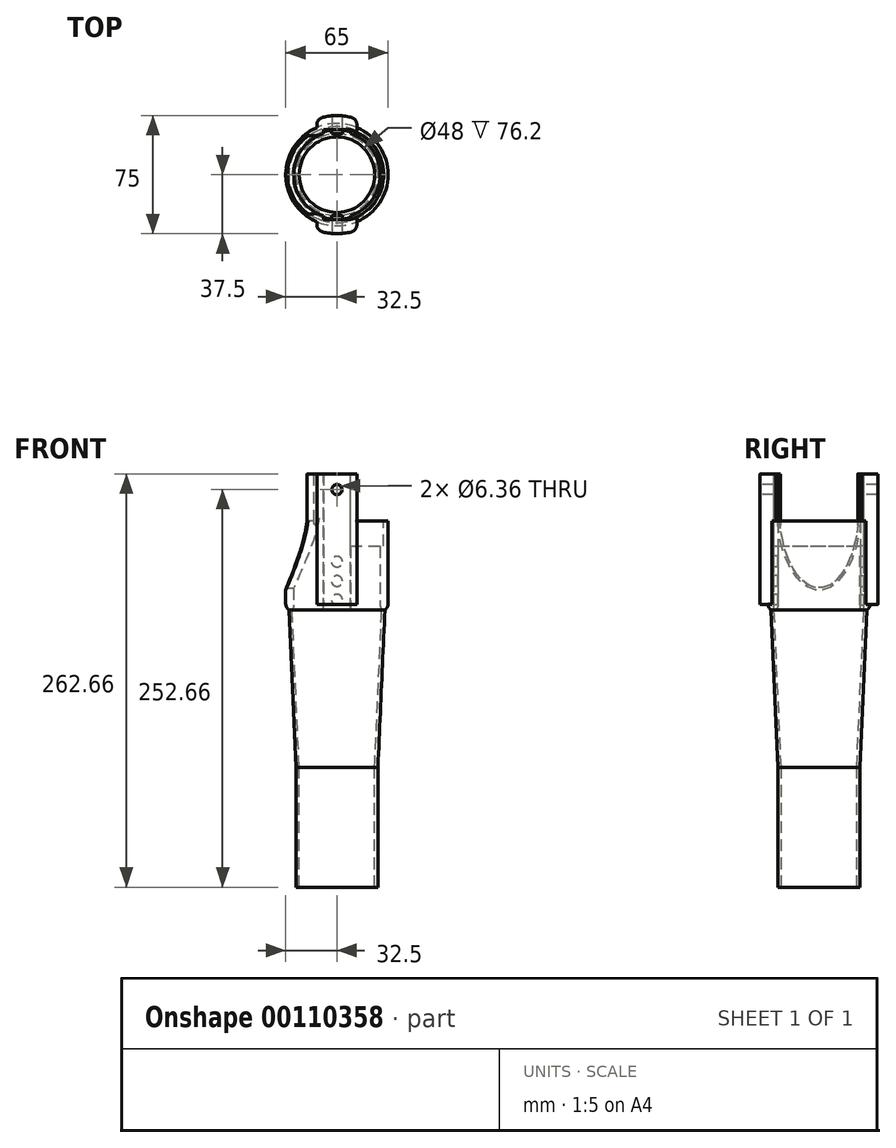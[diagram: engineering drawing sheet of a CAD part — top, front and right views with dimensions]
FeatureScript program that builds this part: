
annotation { "Feature Type Name" : "Feature", "Feature Type Description" : "" }
export const myFeature = defineFeature(function(context is Context, id is Id, definition is map)
    precondition{}
    {
        {
            var Q0;
            Q0=qCreatedBy(makeId("Top.planeOp"),FACE);
            var sketch = newSketch(context, id + "F0", { "sketchPlane" : qUnion([Q0])});
            skCircle(sketch, "E0", {"center": v(0, 0) * mm, "radius": 26 * mm});
            skSolve(sketch);
        }
        {
            var Q0;
            Q0=makeQuery(id+"F0.imprint","IMPRINT",FACE,{"disambiguationData":[TD([[makeQuery(id+"F0.imprint","IMPRINT",EDGE,{"derivedFrom":sQuery(id+"F0.wireOp",EDGE,"E0")}),1.0]])]});
            extrude(context, id + "F1", {"entities" : qUnion([Q0]), "depth" : 76.2 * mm});
        }
        {
            var Q0;
            Q0=makeQuery(id+"F1.opExtrude","CAP_FACE",FACE,{"disambiguationData":[OSD([sQuery(id+"F0.wireOp",EDGE,"E0")])],"isStart":false});
            cPlane(context, id + "F2", {"entities" : qUnion([Q0]), "cplaneType" : CPlaneType.OFFSET, "offset" : 0 * mm, "width" : 150 * mm, "height" : 150 * mm});
        }
        {
            var Q0;
            Q0=qCreatedBy(id+"F2.planeOp",FACE);
            var sketch = newSketch(context, id + "F3", { "sketchPlane" : qUnion([Q0])});
            skCircle(sketch, "E1.0", {"center": v(0, 0) * mm, "radius": 26 * mm});
            skSolve(sketch);
        }
        {
            var Q0;
            Q0=qCreatedBy(id+"F2.planeOp",FACE);
            cPlane(context, id + "F4", {"entities" : qUnion([Q0]), "cplaneType" : CPlaneType.OFFSET, "offset" : 100 * mm, "width" : 150 * mm, "height" : 150 * mm});
        }
        {
            var Q0;
            Q0=qCreatedBy(id+"F4.planeOp",FACE);
            var sketch = newSketch(context, id + "F5", { "sketchPlane" : qUnion([Q0])});
            skCircle(sketch, "E2", {"center": v(0, 0) * mm, "radius": 30.5 * mm});
            skSolve(sketch);
        }
        {
            var Q1;
            Q1=makeQuery(id+"F3.imprint","IMPRINT",FACE,{"disambiguationData":[TD([[makeQuery(id+"F3.imprint","IMPRINT",EDGE,{"derivedFrom":sQuery(id+"F3.wireOp",EDGE,"E1.0")}),1.0]])]});
            var Q2;
            Q2=makeQuery(id+"F5.imprint","IMPRINT",FACE,{"disambiguationData":[TD([[makeQuery(id+"F5.imprint","IMPRINT",EDGE,{"derivedFrom":sQuery(id+"F5.wireOp",EDGE,"E2")}),1.0]])]});
            loft(context, id + "F6", {"operationType" : NewBodyOperationType.ADD, "sheetProfilesArray" : [{ "sheetProfileEntities" : qUnion([Q1]) }, { "sheetProfileEntities" : qUnion([Q2]) }]});
        }
        {
            var Q0;
            Q0=qCreatedBy(id+"F2.planeOp",FACE);
            var sketch = newSketch(context, id + "F7", { "sketchPlane" : qUnion([Q0])});
            skCircle(sketch, "E3", {"center": v(0, 0) * mm, "radius": 24 * mm});
            skSolve(sketch);
        }
        {
            var Q0;
            Q0=qCreatedBy(id+"F4.planeOp",FACE);
            var sketch = newSketch(context, id + "F8", { "sketchPlane" : qUnion([Q0])});
            skCircle(sketch, "E4", {"center": v(0, 0) * mm, "radius": 28.5 * mm});
            skSolve(sketch);
        }
        {
            var Q1;
            Q1=makeQuery(id+"F8.imprint","IMPRINT",FACE,{"disambiguationData":[TD([[makeQuery(id+"F8.imprint","IMPRINT",EDGE,{"derivedFrom":sQuery(id+"F8.wireOp",EDGE,"E4")}),1.0]])]});
            var Q2;
            Q2=qSketchRegion(id+"F7",true);
            loft(context, id + "F9", {"operationType" : NewBodyOperationType.REMOVE, "sheetProfilesArray" : [{ "sheetProfileEntities" : qUnion([Q1]) }, { "sheetProfileEntities" : qUnion([Q2]) }]});
        }
        {
            var Q0;
            Q0=qCreatedBy(makeId("Top.planeOp"),FACE);
            var sketch = newSketch(context, id + "F10", { "sketchPlane" : qUnion([Q0])});
            skCircle(sketch, "E5", {"center": v(0, 0) * mm, "radius": 24 * mm});
            skSolve(sketch);
        }
        {
            var Q1;
            Q1=qSketchRegion(id+"F7",true);
            var Q2;
            Q2=qSketchRegion(id+"F10",true);
            loft(context, id + "F11", {"operationType" : NewBodyOperationType.REMOVE, "sheetProfilesArray" : [{ "sheetProfileEntities" : qUnion([Q1]) }, { "sheetProfileEntities" : qUnion([Q2]) }]});
        }
        {
            var Q0;
            Q0=qCreatedBy(id+"F4.planeOp",FACE);
            var sketch = newSketch(context, id + "F12", { "sketchPlane" : qUnion([Q0])});
            skCircle(sketch, "E6", {"center": v(0, 0) * mm, "radius": 32.5 * mm});
            skCircle(sketch, "E7.0", {"center": v(0, 0) * mm, "radius": 27.5 * mm});
            skSolve(sketch);
        }
        {
            var Q0;
            Q0=qSketchRegion(id+"F12",true);
            extrude(context, id + "F13", {"entities" : qUnion([Q0]), "operationType" : NewBodyOperationType.ADD, "depth" : 56.46 * mm});
        }
        {
            var Q0;
            Q0=makeQuery(id+"F13.opExtrude","CAP_EDGE",EDGE,{"disambiguationData":[OSD([sQuery(id+"F12.wireOp",EDGE,"E6")])],"isStart":true});
            fillet(context, id + "F14", {"entities" : qUnion([Q0]), "radius" : 5 * mm, "tangentPropagation" : true, "allowEdgeOverflow" : false});
        }
        {
            var Q0;
            Q0=makeQuery(id+"F13.opExtrude","CAP_FACE",FACE,{"disambiguationData":[OSD([sQuery(id+"F12.wireOp",EDGE,"E6"),sQuery(id+"F12.wireOp",EDGE,"E7.0")])],"isStart":false});
            cPlane(context, id + "F15", {"entities" : qUnion([Q0]), "cplaneType" : CPlaneType.OFFSET, "offset" : 0 * mm, "width" : 150 * mm, "height" : 150 * mm});
        }
        {
            var Q0;
            Q0=qCreatedBy(id+"F15.planeOp",FACE);
            var sketch = newSketch(context, id + "F16", { "sketchPlane" : qUnion([Q0])});
            skCircle(sketch, "E8.0", {"center": v(0, 0) * mm, "radius": 32.5 * mm, "construction": true});
            skCircle(sketch, "E9.0", {"center": v(0, 0) * mm, "radius": 27.5 * mm, "construction": true});
            skArc(sketch, "E10", {"start": v(8.5, -28.5) * mm, "mid": v(29.74, 0) * mm, "end": v(8.5, 28.5) * mm});
            skArc(sketch, "E11", {"start": v(8.5, -24.3) * mm, "mid": v(25.75, 0) * mm, "end": v(8.5, 24.3) * mm});
            skLineSegment(sketch, "E12", {"start": v(8.5, 28.5) * mm, "end": v(8.5, 24.3) * mm});
            skLineSegment(sketch, "E13.MirrorCS", {"start": v(8.5, -28.5) * mm, "end": v(8.5, -24.3) * mm});
            skPoint(sketch, "E14.orphan", {"position": v(0, 29.74) * mm});
            skPoint(sketch, "E15.orphan", {"position": v(0, -25.75) * mm});
            skSolve(sketch);
        }
        {
            var Q0;
            Q0=qSketchRegion(id+"F16",true);
            extrude(context, id + "F17", {"entities" : qUnion([Q0]), "operationType" : NewBodyOperationType.REMOVE, "oppositeDirection" : true, "depth" : 16 * mm});
        }
        {
            var Q0;
            Q0=qCreatedBy(id+"F15.planeOp",FACE);
            var sketch = newSketch(context, id + "F18", { "sketchPlane" : qUnion([Q0])});
            skLineSegment(sketch, "E16.bottom", {"start": v(-8.5, 28.5) * mm, "end": v(8.5, 28.5) * mm});
            skLineSegment(sketch, "E16.top", {"start": v(-8.5, 24) * mm, "end": v(8.5, 24) * mm});
            skLineSegment(sketch, "E16.left", {"start": v(-8.5, 28.5) * mm, "end": v(-8.5, 24) * mm});
            skLineSegment(sketch, "E16.right", {"start": v(8.5, 28.5) * mm, "end": v(8.5, 24) * mm});
            skLineSegment(sketch, "E17", {"start": v(0, 28.5) * mm, "end": v(0, 24) * mm, "construction": true});
            skLineSegment(sketch, "E18.0", {"start": v(8.5, -28.5) * mm, "end": v(8.5, -28.5) * mm});
            skLineSegment(sketch, "E19.MirrorCS", {"start": v(-8.5, -24) * mm, "end": v(8.5, -24) * mm});
            skLineSegment(sketch, "E20.MirrorCS", {"start": v(8.5, -28.5) * mm, "end": v(8.5, -24) * mm});
            skLineSegment(sketch, "E21.MirrorCS", {"start": v(-8.5, -28.5) * mm, "end": v(8.5, -28.5) * mm});
            skLineSegment(sketch, "E22.MirrorCS", {"start": v(-8.5, -28.5) * mm, "end": v(-8.5, -24) * mm});
            skSolve(sketch);
        }
        {
            var Q0;
            Q0=qSketchRegion(id+"F18",true);
            extrude(context, id + "F19", {"entities" : qUnion([Q0]), "operationType" : NewBodyOperationType.REMOVE, "oppositeDirection" : true, "depth" : 56.46 * mm});
        }
        {
            var Q0;
            {var subQ0=sQuery(id+"F12.wireOp",EDGE,"E7.0");Q0=makeQuery(id+"F19.boolean.opBoolean","SPLIT",EDGE,{"disambiguationData":[TD([makeQuery(id+"F19.opExtrude","SWEPT_FACE",FACE,{"disambiguationData":[OSD([sQuery(id+"F18.wireOp",EDGE,"E16.left")])]})])],"derivedFrom":makeQuery(id+"F13.opExtrude","CAP_EDGE",EDGE,{"disambiguationData":[OSD([subQ0])],"isStart":true})});}
            var Q1;
            {var subQ0=sQuery(id+"F12.wireOp",EDGE,"E7.0");Q1=makeQuery(id+"F19.boolean.opBoolean","SPLIT",EDGE,{"disambiguationData":[TD([makeQuery(id+"F19.opExtrude","SWEPT_FACE",FACE,{"disambiguationData":[OSD([sQuery(id+"F18.wireOp",EDGE,"E16.right")])]})])],"derivedFrom":makeQuery(id+"F13.opExtrude","CAP_EDGE",EDGE,{"disambiguationData":[OSD([subQ0])],"isStart":true})});}
            fillet(context, id + "F20", {"entities" : qUnion([Q0, Q1]), "radius" : 5 * mm, "tangentPropagation" : true, "allowEdgeOverflow" : false});
        }
        {
            var Q0;
            Q0=makeQuery(id+"F19.boolean.opBoolean","COPY",FACE,{"derivedFrom":makeQuery(id+"F19.opExtrude","SWEPT_FACE",FACE,{"disambiguationData":[OSD([sQuery(id+"F18.wireOp",EDGE,"E16.bottom")])]})});
            cPlane(context, id + "F21", {"entities" : qUnion([Q0]), "cplaneType" : CPlaneType.OFFSET, "offset" : 0 * mm, "width" : 150 * mm, "height" : 150 * mm});
        }
        {
            var Q0;
            Q0=qCreatedBy(id+"F21.planeOp",FACE);
            var sketch = newSketch(context, id + "F22", { "sketchPlane" : qUnion([Q0])});
            skLineSegment(sketch, "E23.0.0", {"start": v(8.5, 232.66) * mm, "end": v(-8.5, 232.66) * mm, "construction": true});
            skLineSegment(sketch, "E23.0.1", {"start": v(-8.5, 232.66) * mm, "end": v(-8.5, 176.2) * mm, "construction": true});
            skLineSegment(sketch, "E23.0.2", {"start": v(-8.5, 176.2) * mm, "end": v(0, 176.2) * mm, "construction": true});
            skLineSegment(sketch, "E23.0.3", {"start": v(0, 176.2) * mm, "end": v(8.5, 176.2) * mm, "construction": true});
            skLineSegment(sketch, "E23.0.4", {"start": v(8.5, 176.2) * mm, "end": v(8.5, 232.66) * mm, "construction": true});
            skLineSegment(sketch, "E24", {"start": v(0, 232.66) * mm, "end": v(0, 176.2) * mm, "construction": true});
            skCircle(sketch, "E25", {"center": v(0, 206.85) * mm, "radius": 3.45 * mm});
            skCircle(sketch, "E26", {"center": v(0, 194.54) * mm, "radius": 3.45 * mm});
            skCircle(sketch, "E27", {"center": v(0, 182.7) * mm, "radius": 3.45 * mm});
            skSolve(sketch);
        }
        {
            var Q0;
            Q0=qSketchRegion(id+"F22",true);
            extrude(context, id + "F23", {"entities" : qUnion([Q0]), "depth" : 2.5 * mm});
        }
        {
            var Q0;
            Q0=makeQuery(id+"F23.opExtrude","SWEPT_BODY",BODY,{"disambiguationData":[OSD([sQuery(id+"F22.wireOp",EDGE,"E25")])]});
            var Q1;
            Q1=makeQuery(id+"F23.opExtrude","SWEPT_BODY",BODY,{"disambiguationData":[OSD([sQuery(id+"F22.wireOp",EDGE,"E26")])]});
            var Q2;
            Q2=makeQuery(id+"F23.opExtrude","SWEPT_BODY",BODY,{"disambiguationData":[OSD([sQuery(id+"F22.wireOp",EDGE,"E27")])]});
            var Q3;
            Q3=qCreatedBy(makeId("Front.planeOp"),FACE);
            mirror(context, id + "F24", {"operationType" : NewBodyOperationType.ADD, "entities" : qUnion([Q0, Q1, Q2]), "mirrorPlane" : qUnion([Q3])});
        }
        {
            var Q0;
            Q0=qCreatedBy(id+"F15.planeOp",FACE);
            var sketch = newSketch(context, id + "F25", { "sketchPlane" : qUnion([Q0])});
            skCircle(sketch, "E28", {"center": v(0, 0) * mm, "radius": 37.5 * mm});
            skCircle(sketch, "E29.0", {"center": v(0, 0) * mm, "radius": 32.5 * mm});
            skLineSegment(sketch, "E30", {"start": v(12.77, 35.26) * mm, "end": v(12.77, 29.89) * mm});
            skLineSegment(sketch, "E31.MirrorCS", {"start": v(-12.77, 35.26) * mm, "end": v(-12.77, 29.89) * mm});
            skLineSegment(sketch, "E32.MirrorCS", {"start": v(12.77, -35.26) * mm, "end": v(12.77, -29.89) * mm});
            skLineSegment(sketch, "E33.MirrorCS", {"start": v(-12.77, -35.26) * mm, "end": v(-12.77, -29.89) * mm});
            skSolve(sketch);
        }
        {
            var Q0;
            {var subQ1=sQuery(id+"F25.wireOp",EDGE,"E30");Q0=makeQuery(id+"F25.imprint","IMPRINT",FACE,{"disambiguationData":[TD([[makeQuery(id+"F25.imprint","IMPRINT",EDGE,{"derivedFrom":subQ1}),-1.0]])]});}
            var Q1;
            {var subQ1=sQuery(id+"F25.wireOp",EDGE,"E32.MirrorCS");Q1=makeQuery(id+"F25.imprint","IMPRINT",FACE,{"disambiguationData":[TD([[makeQuery(id+"F25.imprint","IMPRINT",EDGE,{"derivedFrom":subQ1}),1.0]])]});}
            extrude(context, id + "F26", {"entities" : qUnion([Q0, Q1]), "operationType" : NewBodyOperationType.ADD, "depth" : 30 * mm, "hasSecondDirection" : true, "secondDirectionOppositeDirection" : true, "secondDirectionDepth" : 53 * mm});
        }
        {
            var Q0;
            Q0=makeQuery(id+"F13.opExtrude","CAP_FACE",FACE,{"disambiguationData":[OSD([sQuery(id+"F12.wireOp",EDGE,"E6"),sQuery(id+"F12.wireOp",EDGE,"E7.0")])],"isStart":false});
            var sketch = newSketch(context, id + "F27", { "sketchPlane" : qUnion([Q0])});
            skLineSegment(sketch, "E34", {"start": v(12.77, 29.89) * mm, "end": v(12.77, 26.86) * mm});
            skLineSegment(sketch, "E35", {"start": v(-12.77, 29.89) * mm, "end": v(-12.77, 24.35) * mm});
            skLineSegment(sketch, "E36.MirrorCS", {"start": v(12.77, -29.89) * mm, "end": v(12.77, -26.86) * mm});
            skLineSegment(sketch, "E37.MirrorCS", {"start": v(-12.77, -29.89) * mm, "end": v(-12.77, -24.35) * mm});
            skSolve(sketch);
        }
        {
            var Q0;
            {var subQ5=sQuery(id+"F27.wireOp",EDGE,"E34");Q0=makeQuery(id+"F27.imprint","IMPRINT",FACE,{"disambiguationData":[TD([[makeQuery(id+"F27.imprint","IMPRINT",EDGE,{"derivedFrom":subQ5}),-1.0]])]});}
            var Q1;
            {var subQ9=sQuery(id+"F27.wireOp",EDGE,"E36.MirrorCS");Q1=makeQuery(id+"F27.imprint","IMPRINT",FACE,{"disambiguationData":[TD([[makeQuery(id+"F27.imprint","IMPRINT",EDGE,{"derivedFrom":subQ9}),1.0]])]});}
            extrude(context, id + "F28", {"entities" : qUnion([Q0, Q1]), "operationType" : NewBodyOperationType.ADD, "depth" : 30 * mm, "hasSecondDirection" : true, "secondDirectionOppositeDirection" : true, "secondDirectionDepth" : 25 * mm});
        }
        {
            var Q0;
            Q0=makeQuery(id+"F26.opExtrude","SWEPT_EDGE",EDGE,{"disambiguationData":[OSD([sQuery(id+"F25.wireOp",EDGE,"E28"),sQuery(id+"F25.wireOp",EDGE,"E31.MirrorCS")])]});
            var Q1;
            Q1=makeQuery(id+"F26.opExtrude","SWEPT_EDGE",EDGE,{"disambiguationData":[OSD([sQuery(id+"F25.wireOp",EDGE,"E28"),sQuery(id+"F25.wireOp",EDGE,"E33.MirrorCS")])]});
            var Q2;
            Q2=makeQuery(id+"F26.opExtrude","SWEPT_EDGE",EDGE,{"disambiguationData":[OSD([sQuery(id+"F25.wireOp",EDGE,"E28"),sQuery(id+"F25.wireOp",EDGE,"E32.MirrorCS")])]});
            var Q3;
            Q3=makeQuery(id+"F26.opExtrude","SWEPT_EDGE",EDGE,{"disambiguationData":[OSD([sQuery(id+"F25.wireOp",EDGE,"E28"),sQuery(id+"F25.wireOp",EDGE,"E30")])]});
            fillet(context, id + "F29", {"entities" : qUnion([Q0, Q1, Q2, Q3]), "radius" : 5 * mm, "tangentPropagation" : true, "allowEdgeOverflow" : false});
        }
        {
            var Q0;
            Q0=makeQuery(id+"F28.opExtrude","SWEPT_EDGE",EDGE,{"disambiguationData":[OSD([sQuery(id+"F12.wireOp",EDGE,"E7.0"),sQuery(id+"F27.wireOp",EDGE,"E37.MirrorCS")])]});
            fillet(context, id + "F30", {"entities" : qUnion([Q0]), "radius" : 1 * mm, "tangentPropagation" : true, "allowEdgeOverflow" : false});
        }
        {
            var Q0;
            Q0=makeQuery(id+"F28.opExtrude","SWEPT_EDGE",EDGE,{"disambiguationData":[OSD([sQuery(id+"F12.wireOp",EDGE,"E7.0"),sQuery(id+"F27.wireOp",EDGE,"E35")])]});
            fillet(context, id + "F31", {"entities" : qUnion([Q0]), "radius" : 1 * mm, "tangentPropagation" : true, "allowEdgeOverflow" : false});
        }
        {
            var Q0;
            Q0=makeQuery(id+"F28.opExtrude","SWEPT_EDGE",EDGE,{"disambiguationData":[OSD([sQuery(id+"F16.wireOp",EDGE,"E10"),sQuery(id+"F27.wireOp",EDGE,"E36.MirrorCS")])]});
            fillet(context, id + "F32", {"entities" : qUnion([Q0]), "radius" : 1 * mm, "tangentPropagation" : true, "allowEdgeOverflow" : false});
        }
        {
            var Q0;
            Q0=makeQuery(id+"F28.opExtrude","SWEPT_EDGE",EDGE,{"disambiguationData":[OSD([sQuery(id+"F16.wireOp",EDGE,"E10"),sQuery(id+"F27.wireOp",EDGE,"E34")])]});
            fillet(context, id + "F33", {"entities" : qUnion([Q0]), "radius" : 1 * mm, "tangentPropagation" : true, "allowEdgeOverflow" : false});
        }
        {
            var Q0;
            {var subQ0=sQuery(id+"F18.wireOp",EDGE,"E16.bottom");Q0=makeQuery(id+"F28.boolean.opBoolean","MERGE",FACE,{"derivedFrom":[makeQuery(id+"F19.boolean.opBoolean","COPY",FACE,{"derivedFrom":makeQuery(id+"F19.opExtrude","SWEPT_FACE",FACE,{"disambiguationData":[OSD([subQ0])]})}),makeQuery(id+"F28.opExtrude","SWEPT_FACE",FACE,{"disambiguationData":[OSD([subQ0])]})]});}
            var sketch = newSketch(context, id + "F34", { "sketchPlane" : qUnion([Q0])});
            skLineSegment(sketch, "E38.0", {"start": v(-8.5, 262.66) * mm, "end": v(8.5, 262.66) * mm, "construction": true});
            skLineSegment(sketch, "E39", {"start": v(0, 262.66) * mm, "end": v(0, 242.66) * mm, "construction": true});
            skPoint(sketch, "E39.endSnap0", {"position": v(0, 262.66) * mm});
            skCircle(sketch, "E40", {"center": v(0, 252.66) * mm, "radius": 3.18 * mm});
            skSolve(sketch);
        }
        {
            var Q0;
            Q0=makeQuery(id+"F34.imprint","IMPRINT",FACE,{"disambiguationData":[TD([[makeQuery(id+"F34.imprint","IMPRINT",EDGE,{"derivedFrom":sQuery(id+"F34.wireOp",EDGE,"E40")}),1.0]])]});
            extrude(context, id + "F35", {"entities" : qUnion([Q0]), "oppositeDirection" : true, "depth" : 15 * mm});
        }
        {
            var Q0;
            Q0=makeQuery(id+"F35.opExtrude","SWEPT_BODY",BODY,{"disambiguationData":[OSD([sQuery(id+"F34.wireOp",EDGE,"E40")])]});
            var Q1;
            Q1=qCreatedBy(makeId("Front.planeOp"),FACE);
            mirror(context, id + "F36", {"operationType" : NewBodyOperationType.ADD, "entities" : qUnion([Q0]), "mirrorPlane" : qUnion([Q1])});
        }
        {
            var Q0;
            Q0=qCreatedBy(makeId("Right.planeOp"),FACE);
            cPlane(context, id + "F37", {"entities" : qUnion([Q0]), "cplaneType" : CPlaneType.OFFSET, "offset" : 55 * mm, "oppositeDirection" : true, "width" : 150 * mm, "height" : 150 * mm});
        }
        {
            var Q0;
            Q0=qCreatedBy(id+"F37.planeOp",FACE);
            var sketch = newSketch(context, id + "F38", { "sketchPlane" : qUnion([Q0])});
            skLineSegment(sketch, "E41", {"start": v(-31.5, 188.04) * mm, "end": v(-31.5, 188.5) * mm, "construction": true});
            skLineSegment(sketch, "E42", {"start": v(31.5, 188.5) * mm, "end": v(31.5, 188.04) * mm, "construction": true});
            skEllipse(sketch, "E43", {"center": v(0, 241.57) * mm, "majorRadius": 25.3 * mm, "minorRadius": 51.5 * mm, "majorAxis": v(-1, 0)});
            skSolve(sketch);
        }
        {
            var Q0;
            Q0=qSketchRegion(id+"F38",true);
            extrude(context, id + "F39", {"entities" : qUnion([Q0]), "operationType" : NewBodyOperationType.REMOVE, "depth" : 40 * mm});
        }
        {
            var Q0;
            Q0=makeQuery(id+"F39.boolean.opBoolean","INTERSECT",EDGE,{"derivedFrom":[makeQuery(id+"F13.opExtrude","SWEPT_FACE",FACE,{"disambiguationData":[OSD([sQuery(id+"F12.wireOp",EDGE,"E6")])]}),makeQuery(id+"F39.opExtrude","SWEPT_FACE",FACE,{"disambiguationData":[OSD([sQuery(id+"F38.wireOp",EDGE,"E43")])]})]});
            fillet(context, id + "F40", {"entities" : qUnion([Q0]), "radius" : 1 * mm, "tangentPropagation" : true, "allowEdgeOverflow" : false});
        }
        {
            var Q0;
            {var subQ0=sQuery(id+"F12.wireOp",EDGE,"E6");var subQ1=sQuery(id+"F12.wireOp",EDGE,"E7.0");var subQ6=sQuery(id+"F25.wireOp",EDGE,"E33.MirrorCS");var subQ7=makeQuery(id+"F26.opExtrude","SWEPT_FACE",FACE,{"disambiguationData":[OSD([subQ6])]});Q0=makeQuery(id+"F39.boolean.opBoolean","SPLIT",FACE,{"disambiguationData":[TD([subQ7])],"derivedFrom":makeQuery(id+"F28.boolean.opBoolean","SPLIT",FACE,{"disambiguationData":[TD([makeQuery(id+"F13.opExtrude","SWEPT_FACE",FACE,{"disambiguationData":[OSD([subQ1])]})])],"derivedFrom":makeQuery(id+"F13.opExtrude","CAP_FACE",FACE,{"disambiguationData":[OSD([subQ0,subQ1])],"isStart":false})})});}
            var Q1;
            {var subQ0=sQuery(id+"F12.wireOp",EDGE,"E6");var subQ1=sQuery(id+"F12.wireOp",EDGE,"E7.0");var subQ6=sQuery(id+"F25.wireOp",EDGE,"E31.MirrorCS");var subQ7=makeQuery(id+"F26.opExtrude","SWEPT_FACE",FACE,{"disambiguationData":[OSD([subQ6])]});Q1=makeQuery(id+"F39.boolean.opBoolean","SPLIT",FACE,{"disambiguationData":[TD([subQ7])],"derivedFrom":makeQuery(id+"F28.boolean.opBoolean","SPLIT",FACE,{"disambiguationData":[TD([makeQuery(id+"F13.opExtrude","SWEPT_FACE",FACE,{"disambiguationData":[OSD([subQ1])]})])],"derivedFrom":makeQuery(id+"F13.opExtrude","CAP_FACE",FACE,{"disambiguationData":[OSD([subQ0,subQ1])],"isStart":false})})});}
            var Q2;
            Q2=makeQuery(id+"F28.boolean.opBoolean","MERGE",FACE,{"derivedFrom":[makeQuery(id+"F26.opExtrude","CAP_FACE",FACE,{"disambiguationData":[OSD([sQuery(id+"F25.wireOp",EDGE,"E28"),sQuery(id+"F25.wireOp",EDGE,"E29.0"),sQuery(id+"F25.wireOp",EDGE,"E32.MirrorCS"),sQuery(id+"F25.wireOp",EDGE,"E33.MirrorCS")])],"isStart":false}),makeQuery(id+"F28.opExtrude","CAP_FACE",FACE,{"disambiguationData":[OSD([sQuery(id+"F12.wireOp",EDGE,"E6"),sQuery(id+"F12.wireOp",EDGE,"E7.0"),sQuery(id+"F16.wireOp",EDGE,"E10"),sQuery(id+"F18.wireOp",EDGE,"E20.MirrorCS"),sQuery(id+"F18.wireOp",EDGE,"E21.MirrorCS"),sQuery(id+"F18.wireOp",EDGE,"E22.MirrorCS"),sQuery(id+"F27.wireOp",EDGE,"E36.MirrorCS"),sQuery(id+"F27.wireOp",EDGE,"E37.MirrorCS")])],"isStart":false})]});
            extrude(context, id + "F41", {"entities" : qUnion([Q0, Q1]), "operationType" : NewBodyOperationType.ADD, "endBound" : BoundingType.UP_TO_SURFACE, "endBoundEntityFace" : qUnion([Q2]), "depth" : 25 * mm});
        }
        {
            var Q0;
            {var subQ0=sQuery(id+"F38.wireOp",EDGE,"E43");var subQ1=makeQuery(id+"F39.opExtrude","CAP_FACE",FACE,{"disambiguationData":[OSD([subQ0])],"isStart":false});var subQ2=sQuery(id+"F12.wireOp",EDGE,"E7.0");var subQ3=makeQuery(id+"F13.opExtrude","SWEPT_FACE",FACE,{"disambiguationData":[OSD([subQ2])]});var subQ5=sQuery(id+"F12.wireOp",EDGE,"E6");var subQ7=makeQuery(id+"F13.opExtrude","CAP_EDGE",EDGE,{"disambiguationData":[OSD([subQ2])],"isStart":false});var subQ8=sQuery(id+"F18.wireOp",EDGE,"E16.left");var subQ9=makeQuery(id+"F28.opExtrude","SWEPT_FACE",FACE,{"disambiguationData":[OSD([subQ2]),TDD([makeQuery(id+"F27.imprint","IMPRINT",EDGE,{"disambiguationData":[TD([[makeQuery(id+"F27.imprint","INTERSECT",VERTEX,{"derivedFrom":[makeQuery(id+"F19.boolean.opBoolean","COPY",EDGE,{"derivedFrom":makeQuery(id+"F19.opExtrude","CAP_EDGE",EDGE,{"disambiguationData":[OSD([subQ8])],"isStart":true})}),subQ7]}),1.0]])],"derivedFrom":subQ7})])]});var subQ10=sQuery(id+"F18.wireOp",EDGE,"E22.MirrorCS");var subQ11=makeQuery(id+"F28.opExtrude","SWEPT_FACE",FACE,{"disambiguationData":[OSD([subQ2]),TDD([makeQuery(id+"F27.imprint","IMPRINT",EDGE,{"disambiguationData":[TD([[makeQuery(id+"F27.imprint","INTERSECT",VERTEX,{"derivedFrom":[makeQuery(id+"F19.boolean.opBoolean","COPY",EDGE,{"derivedFrom":makeQuery(id+"F19.opExtrude","CAP_EDGE",EDGE,{"disambiguationData":[OSD([subQ10])],"isStart":true})}),subQ7]}),-1.0]])],"derivedFrom":subQ7})])]});var subQ12=makeQuery(id+"F13.opExtrude","CAP_FACE",FACE,{"disambiguationData":[OSD([subQ5,subQ2])],"isStart":false});var subQ13=makeQuery(id+"F28.boolean.opBoolean","MERGE",FACE,{"derivedFrom":[makeQuery(id+"F19.boolean.opBoolean","SPLIT",FACE,{"disambiguationData":[TD([makeQuery(id+"F19.opExtrude","SWEPT_FACE",FACE,{"disambiguationData":[OSD([subQ8])]})])],"derivedFrom":subQ3}),subQ9,subQ11]});Q0=makeQuery(id+"F41.boolean.opBoolean","MERGE",EDGE,{"derivedFrom":[makeQuery(id+"F39.boolean.opBoolean","INTERSECT",EDGE,{"disambiguationData":[OD(0.0)],"derivedFrom":[subQ13,subQ1]}),makeQuery(id+"F41.opExtrude","SWEPT_EDGE",EDGE,{"disambiguationData":[OSD([subQ5,subQ2,subQ0]),TDD([makeQuery(id+"F39.boolean.opBoolean","INTERSECT",VERTEX,{"disambiguationData":[OD(0.0)],"derivedFrom":[subQ13,makeQuery(id+"F28.boolean.opBoolean","SPLIT",FACE,{"disambiguationData":[TD([subQ3])],"derivedFrom":subQ12}),subQ1]})])]})]});}
            var Q1;
            {var subQ0=sQuery(id+"F38.wireOp",EDGE,"E43");var subQ1=makeQuery(id+"F39.opExtrude","CAP_FACE",FACE,{"disambiguationData":[OSD([subQ0])],"isStart":false});var subQ2=sQuery(id+"F12.wireOp",EDGE,"E7.0");var subQ3=makeQuery(id+"F13.opExtrude","SWEPT_FACE",FACE,{"disambiguationData":[OSD([subQ2])]});var subQ5=sQuery(id+"F12.wireOp",EDGE,"E6");var subQ7=makeQuery(id+"F13.opExtrude","CAP_EDGE",EDGE,{"disambiguationData":[OSD([subQ2])],"isStart":false});var subQ8=sQuery(id+"F18.wireOp",EDGE,"E16.left");var subQ9=makeQuery(id+"F28.opExtrude","SWEPT_FACE",FACE,{"disambiguationData":[OSD([subQ2]),TDD([makeQuery(id+"F27.imprint","IMPRINT",EDGE,{"disambiguationData":[TD([[makeQuery(id+"F27.imprint","INTERSECT",VERTEX,{"derivedFrom":[makeQuery(id+"F19.boolean.opBoolean","COPY",EDGE,{"derivedFrom":makeQuery(id+"F19.opExtrude","CAP_EDGE",EDGE,{"disambiguationData":[OSD([subQ8])],"isStart":true})}),subQ7]}),1.0]])],"derivedFrom":subQ7})])]});var subQ10=sQuery(id+"F18.wireOp",EDGE,"E22.MirrorCS");var subQ11=makeQuery(id+"F28.opExtrude","SWEPT_FACE",FACE,{"disambiguationData":[OSD([subQ2]),TDD([makeQuery(id+"F27.imprint","IMPRINT",EDGE,{"disambiguationData":[TD([[makeQuery(id+"F27.imprint","INTERSECT",VERTEX,{"derivedFrom":[makeQuery(id+"F19.boolean.opBoolean","COPY",EDGE,{"derivedFrom":makeQuery(id+"F19.opExtrude","CAP_EDGE",EDGE,{"disambiguationData":[OSD([subQ10])],"isStart":true})}),subQ7]}),-1.0]])],"derivedFrom":subQ7})])]});var subQ12=makeQuery(id+"F13.opExtrude","CAP_FACE",FACE,{"disambiguationData":[OSD([subQ5,subQ2])],"isStart":false});var subQ13=makeQuery(id+"F28.boolean.opBoolean","MERGE",FACE,{"derivedFrom":[makeQuery(id+"F19.boolean.opBoolean","SPLIT",FACE,{"disambiguationData":[TD([makeQuery(id+"F19.opExtrude","SWEPT_FACE",FACE,{"disambiguationData":[OSD([subQ8])]})])],"derivedFrom":subQ3}),subQ9,subQ11]});Q1=makeQuery(id+"F41.boolean.opBoolean","MERGE",EDGE,{"derivedFrom":[makeQuery(id+"F39.boolean.opBoolean","INTERSECT",EDGE,{"disambiguationData":[OD(1.0)],"derivedFrom":[subQ13,subQ1]}),makeQuery(id+"F41.opExtrude","SWEPT_EDGE",EDGE,{"disambiguationData":[OSD([subQ5,subQ2,subQ0]),TDD([makeQuery(id+"F39.boolean.opBoolean","INTERSECT",VERTEX,{"disambiguationData":[OD(1.0)],"derivedFrom":[subQ13,makeQuery(id+"F28.boolean.opBoolean","SPLIT",FACE,{"disambiguationData":[TD([subQ3])],"derivedFrom":subQ12}),subQ1]})])]})]});}
            fillet(context, id + "F42", {"entities" : qUnion([Q0, Q1]), "radius" : 5 * mm, "tangentPropagation" : true, "allowEdgeOverflow" : false});
        }
        {
            var Q0;
            Q0=makeQuery(id+"F36.opPattern","COPY",FACE,{"derivedFrom":makeQuery(id+"F35.opExtrude","CAP_FACE",FACE,{"disambiguationData":[OSD([sQuery(id+"F34.wireOp",EDGE,"E40")])],"isStart":false}),"instanceName":"1"});
            extrude(context, id + "F43", {"entities" : qUnion([Q0]), "operationType" : NewBodyOperationType.REMOVE, "endBound" : BoundingType.THROUGH_ALL, "oppositeDirection" : true, "depth" : 121.16 * mm});
        }
    });
